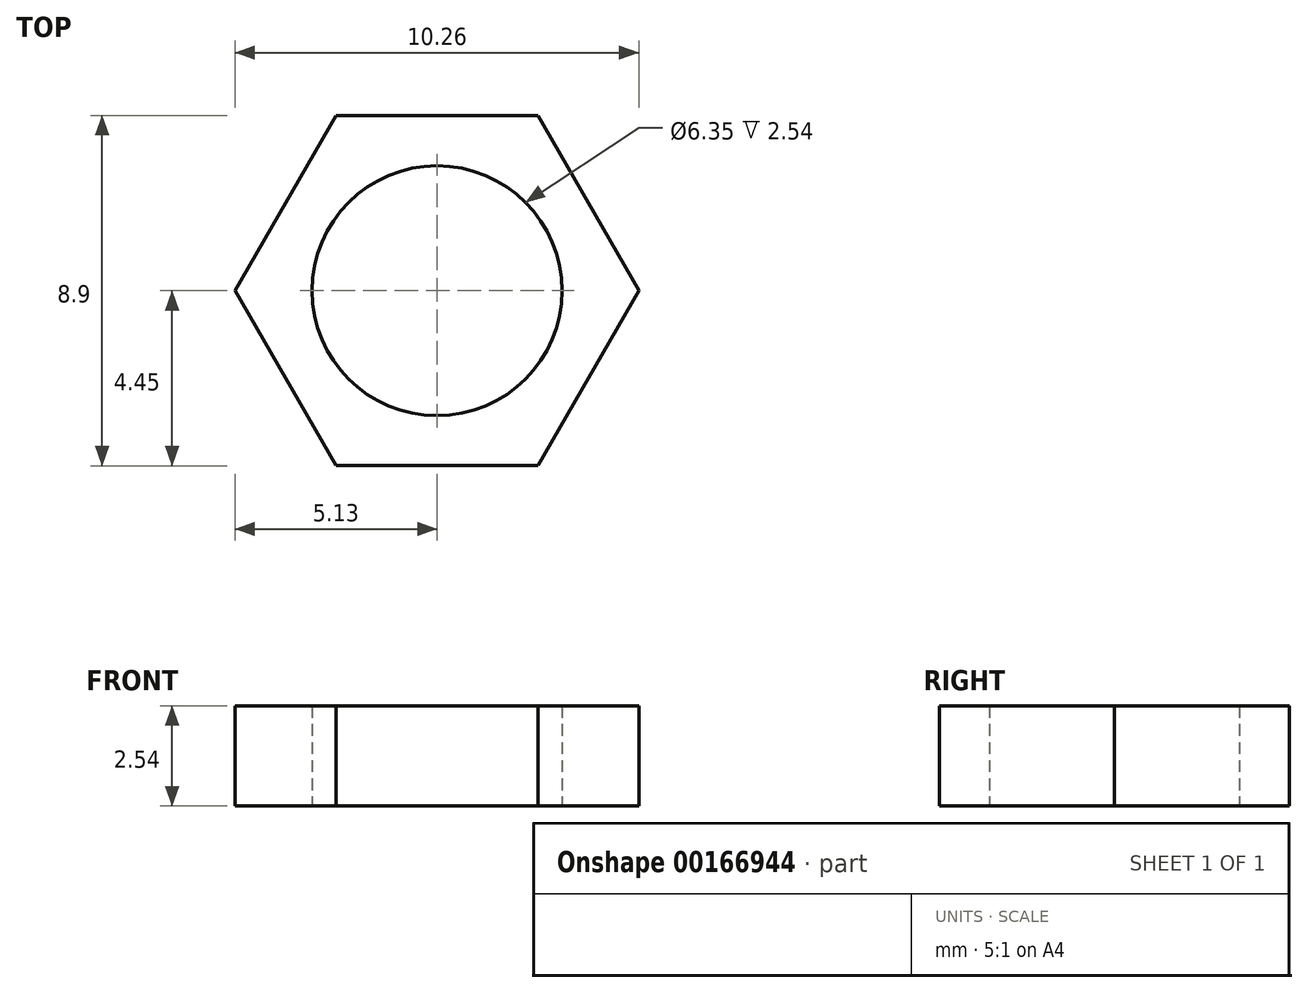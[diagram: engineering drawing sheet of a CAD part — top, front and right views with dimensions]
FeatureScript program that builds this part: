
annotation { "Feature Type Name" : "Feature", "Feature Type Description" : "" }
export const myFeature = defineFeature(function(context is Context, id is Id, definition is map)
    precondition{}
    {
        {
            var Q0;
            Q0=qCreatedBy(makeId("Top.planeOp"),FACE);
            var sketch = newSketch(context, id + "F0", { "sketchPlane" : qUnion([Q0])});
            skCircle(sketch, "E0.cCircle", {"center": v(0, 0) * mm, "radius": 4.45 * mm, "construction": true});
            skLineSegment(sketch, "E0.0", {"start": v(-2.57, 4.45) * mm, "end": v(2.57, 4.45) * mm});
            skLineSegment(sketch, "E0.1", {"start": v(2.57, 4.45) * mm, "end": v(5.13, 0) * mm});
            skLineSegment(sketch, "E0.2", {"start": v(5.13, 0) * mm, "end": v(2.57, -4.44) * mm});
            skLineSegment(sketch, "E0.3", {"start": v(2.57, -4.44) * mm, "end": v(-2.57, -4.45) * mm});
            skLineSegment(sketch, "E0.4", {"start": v(-2.57, -4.45) * mm, "end": v(-5.13, 0) * mm});
            skLineSegment(sketch, "E0.5", {"start": v(-5.13, 0) * mm, "end": v(-2.57, 4.45) * mm});
            skPoint(sketch, "E0.0.midPoint", {"position": v(0, 4.45) * mm});
            skCircle(sketch, "E1", {"center": v(0, 0) * mm, "radius": 3.18 * mm});
            skSolve(sketch);
        }
        {
            var Q0;
            Q0=makeQuery(id+"F0.imprint","IMPRINT",FACE,{"disambiguationData":[TD([[makeQuery(id+"F0.imprint","IMPRINT",EDGE,{"derivedFrom":sQuery(id+"F0.wireOp",EDGE,"E0.0")}),-1.0]])]});
            extrude(context, id + "F1", {"entities" : qUnion([Q0]), "depth" : 2.54 * mm});
        }
    });
